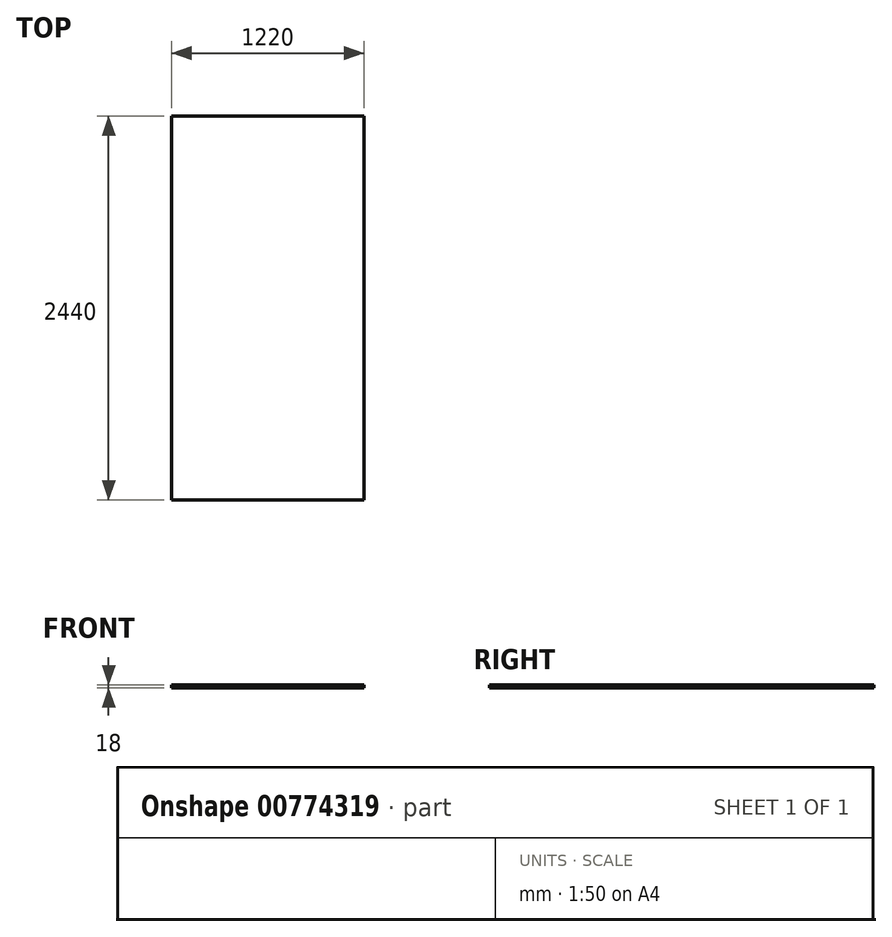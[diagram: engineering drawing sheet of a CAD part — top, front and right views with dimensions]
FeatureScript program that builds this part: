
annotation { "Feature Type Name" : "Feature", "Feature Type Description" : "" }
export const myFeature = defineFeature(function(context is Context, id is Id, definition is map)
    precondition{}
    {
        {
            var Q0;
            Q0=qCreatedBy(makeId("Top.planeOp"),FACE);
            var sketch = newSketch(context, id + "F0", { "sketchPlane" : qUnion([Q0])});
            skLineSegment(sketch, "E0.bottom", {"start": v(610, 1220) * mm, "end": v(-610, 1220) * mm});
            skLineSegment(sketch, "E0.top", {"start": v(610, -1220) * mm, "end": v(-610, -1220) * mm});
            skLineSegment(sketch, "E0.right", {"start": v(-610, 1220) * mm, "end": v(-610, -1220) * mm});
            skPoint(sketch, "E0.middle", {"position": v(0, 0) * mm});
            skLineSegment(sketch, "E1", {"start": v(610, 1220) * mm, "end": v(610, -1220) * mm});
            skSolve(sketch);
        }
        {
            var Q0;
            Q0=makeQuery(id+"F0.imprint","IMPRINT",FACE,{"disambiguationData":[TD([[makeQuery(id+"F0.imprint","IMPRINT",EDGE,{"derivedFrom":sQuery(id+"F0.wireOp",EDGE,"E0.bottom")}),1.0]])]});
            extrude(context, id + "F1", {"entities" : qUnion([Q0]), "depth" : 18 * mm, "offsetDistance" : 25 * mm});
        }
    });
